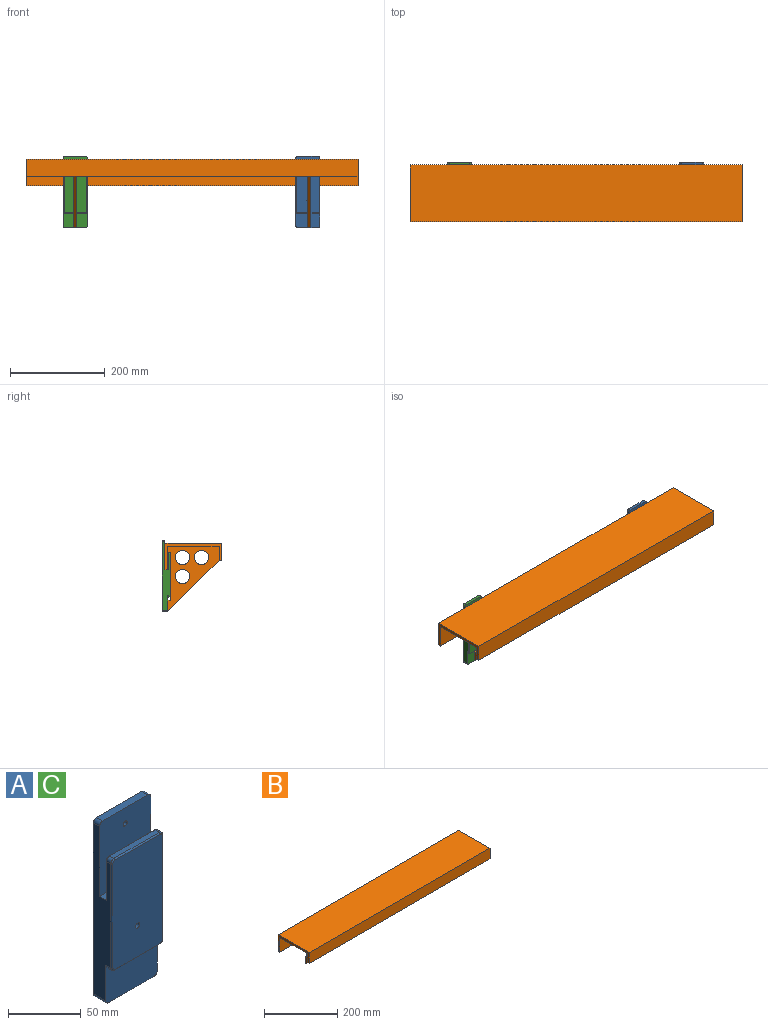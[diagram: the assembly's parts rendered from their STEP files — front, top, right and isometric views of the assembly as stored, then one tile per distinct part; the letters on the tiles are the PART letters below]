
ASSEMBLY  parts=3 mates=1
PART A: 35 faces, bbox 50.5x18x150 mm
  f0: plane 50x33mm, normal (0,-1,0), area 1500mm2, adj f1,f3,f5,f11,f14,f15,f20,f21
  f1: plane 144x17mm, normal (1,0,0), area 1781mm2, adj f0,f7,f8,f9,f14,f16,f18,f21
  f2: plane 44x6mm, normal (0,0,1), area 264mm2, adj f7,f8,f18,f19
  f3: plane 144x17mm, normal (-1,0,0), area 1781mm2, adj f0,f7,f8,f9,f15,f17,f19,f20
  f4: cylinder r=2mm len=6mm, axis (0,1,0), area 75.4mm2, adj f7,f8
  f5: plane 44x12mm, normal (0,0,-1), area 528mm2, adj f0,f8,f20,f21
  f6: cylinder r=2mm len=18mm, axis (0,1,0), area 226.2mm2, adj f8,f13
  f7: plane 62x50mm, normal (0,-1,0), area 3083.6mm2, adj f1,f2,f3,f4,f9,f18,f19
  f8: plane 150x50mm, normal (0,1,0), area 7467.1mm2, adj f1,f2,f3,f4,f5,f6,f18,f19
  f9: plane 50x7mm, normal (0,0,1), area 300.4mm2, adj f1,f3,f7,f10,f30,f34
  f10: plane 48x35mm, normal (0,1,0), area 1678.3mm2, adj f9,f30,f31,f32,f33,f34
  f11: plane 44x5mm, normal (0,0,-1), area 220mm2, adj f0,f14,f15,f29
  f12: plane 44x4mm, normal (0,0,1), area 176mm2, adj f16,f17,f22,f32
  f13: plane 92x48mm, normal (0,-1,0), area 4400mm2, adj f6,f22,f23,f24,f25,f26,f27,f28
  f14: cylinder r=3mm len=5mm, axis (0,1,0), area 23.6mm2, adj f0,f1,f11,f27
  f15: cylinder r=3mm len=5mm, axis (0,-1,0), area 23.6mm2, adj f0,f3,f11,f28
  f16: cylinder r=3mm len=4mm, axis (0,-1,0), area 18.8mm2, adj f1,f12,f23,f33
  f17: cylinder r=3mm len=4mm, axis (0,1,0), area 18.8mm2, adj f3,f12,f24,f31
  f18: cylinder r=3mm len=6mm, axis (0,-1,0), area 28.3mm2, adj f1,f2,f7,f8
  f19: cylinder r=3mm len=6mm, axis (0,1,0), area 28.3mm2, adj f2,f3,f7,f8
  f20: cylinder r=3mm len=12mm, axis (0,-1,0), area 56.5mm2, adj f0,f3,f5,f8
  f21: cylinder r=3mm len=12mm, axis (0,1,0), area 56.5mm2, adj f0,f1,f5,f8
  f22: cylinder r=1mm len=44mm, axis (1,0,0), area 69.1mm2, adj f12,f13,f23,f24
  f23: torus R=2mm, axis (0,-1,0), area 6.5mm2, adj f13,f16,f22,f25
  f24: torus R=2mm, axis (0,-1,0), area 6.5mm2, adj f13,f17,f22,f26
  f25: cylinder r=1mm len=88mm, axis (0,0,-1), area 138.2mm2, adj f1,f13,f23,f27
  f26: cylinder r=1mm len=88mm, axis (0,0,1), area 138.2mm2, adj f3,f13,f24,f28
  f27: torus R=2mm, axis (0,-1,0), area 6.5mm2, adj f13,f14,f25,f29
  f28: torus R=2mm, axis (0,-1,0), area 6.5mm2, adj f13,f15,f26,f29
  f29: cylinder r=1mm len=44mm, axis (-1,0,0), area 69.1mm2, adj f11,f13,f27,f28
  f30: cylinder r=1mm len=33mm, axis (0,0,-1), area 51.8mm2, adj f3,f9,f10,f31
  f31: torus R=2mm, axis (0,-1,0), area 6.5mm2, adj f10,f17,f30,f32
  f32: cylinder r=1mm len=44mm, axis (-1,0,0), area 69.1mm2, adj f10,f12,f31,f33
  f33: torus R=2mm, axis (0,-1,0), area 6.5mm2, adj f10,f16,f32,f34
  f34: cylinder r=1mm len=33mm, axis (0,0,1), area 51.8mm2, adj f1,f9,f10,f33
PART B: 34 faces, bbox 700x120x144 mm
  f0: plane 100x30mm, normal (0,1,0), area 3000mm2, adj f1,f9,f10,f20
  f1: plane 108x100mm, normal (0,0,-1), area 10800mm2, adj f0,f2,f10,f20
  f2: plane 700x50mm, normal (0,-1,0), area 34832mm2, adj f1,f4,f5,f10,f18,f19,f20,f22
  f3: plane 488x30mm, normal (0,1,0), area 14640mm2, adj f4,f9,f19,f32
  f4: plane 488x108mm, normal (0,0,-1), area 52704mm2, adj f2,f3,f19,f32
  f5: plane 700x6mm, normal (0,0,-1), area 4200mm2, adj f2,f6,f10,f23
  f6: plane 700x56mm, normal (0,1,0), area 39200mm2, adj f5,f7,f10,f23
  f7: plane 700x120mm, normal (0,0,1), area 84000mm2, adj f6,f8,f10,f23
  f8: plane 700x36mm, normal (0,-1,0), area 25200mm2, adj f7,f9,f10,f23
  f9: plane 700x6mm, normal (0,0,-1), area 4200mm2, adj f0,f3,f8,f10,f11,f21,f23,f24
  f10: plane 120x56mm, normal (-1,0,0), area 1200mm2, adj f0,f1,f2,f5,f6,f7,f8,f9
  f11: plane 108x108mm, normal (0,-0.71,-0.71), area 916.4mm2, adj f9,f12,f19,f20
  f12: plane 24x6mm, normal (0,1,0), area 144mm2, adj f11,f13,f19,f20
  f13: plane 6x6mm, normal (0,0,1), area 36mm2, adj f12,f14,f19,f20
  f14: plane 100x6mm, normal (0,1,0), area 600mm2, adj f13,f18,f19,f20
  f15: cylinder r=15mm len=30mm, axis (-1,0,0), area 565.5mm2, adj f19,f20
  f16: cylinder r=15mm len=30mm, axis (-1,0,0), area 565.5mm2, adj f19,f20
  f17: cylinder r=15mm len=30mm, axis (-1,0,0), area 565.5mm2, adj f19,f20
  f18: plane 6x6mm, normal (0,0,-1), area 36mm2, adj f2,f14,f19,f20
  f19: plane 138x108mm, normal (1,0,0), area 6351.4mm2, adj f2,f3,f4,f11,f12,f13,f14,f15
  f20: plane 138x108mm, normal (-1,0,0), area 6351.4mm2, adj f0,f1,f2,f11,f12,f13,f14,f15
  f21: plane 100x30mm, normal (0,1,0), area 3000mm2, adj f9,f22,f23,f33
  f22: plane 108x100mm, normal (0,0,-1), area 10800mm2, adj f2,f21,f23,f33
  f23: plane 120x56mm, normal (1,0,0), area 1200mm2, adj f2,f5,f6,f7,f8,f9,f21,f22
  f24: plane 108x108mm, normal (0,-0.71,-0.71), area 916.4mm2, adj f9,f25,f32,f33
  f25: plane 24x6mm, normal (0,1,0), area 144mm2, adj f24,f26,f32,f33
  f26: plane 6x6mm, normal (0,0,1), area 36mm2, adj f25,f27,f32,f33
  f27: plane 100x6mm, normal (0,1,0), area 600mm2, adj f26,f31,f32,f33
  f28: cylinder r=15mm len=30mm, axis (1,0,0), area 565.5mm2, adj f32,f33
  f29: cylinder r=15mm len=30mm, axis (1,0,0), area 565.5mm2, adj f32,f33
  f30: cylinder r=15mm len=30mm, axis (1,0,0), area 565.5mm2, adj f32,f33
  f31: plane 6x6mm, normal (0,0,-1), area 36mm2, adj f2,f27,f32,f33
  f32: plane 138x108mm, normal (-1,0,0), area 6351.4mm2, adj f2,f3,f4,f24,f25,f26,f27,f28
  f33: plane 138x108mm, normal (1,0,0), area 6351.4mm2, adj f2,f21,f22,f24,f25,f26,f27,f28
PART C: same geometry as A
PLACE A t=(477.91,112.85,205.16)mm
PLACE B t=(-16.36,46.85,271.16)mm
PLACE C t=(-12.09,112.85,205.16)mm
MATE slider B.f10 <-> C.f3  axis (-1,0,0) through (-116.36,106.85,218.16)mm
